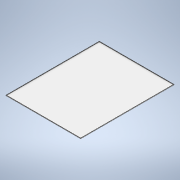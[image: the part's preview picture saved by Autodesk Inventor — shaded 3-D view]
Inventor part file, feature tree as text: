
AUTODESK INVENTOR PART (.ipt)
format: ipt  version: 2021 (Build 250183000, 183)  size: 107,520 bytes
history: native  units: mm
features: extrude x2, sketch x2
ambient origin geometry x8: Origin, YZ Plane, XZ Plane, XY Plane, X Axis, Y Axis, Z Axis, Center Point
bodies: Solid1 (feature_tree)
feature tree (4):
  extrude  "Extrusion1"  Depth=1600.0mm
  extrude  "Extrusion2"  Depth=5.0mm
  sketch  "Sketch1"  dims[d0=2000.0mm d1=1600.0mm]
  sketch  "Sketch2"  dims[d2=12.0mm d3=0.0mm d4=5.0mm d5=10.0mm d6=0.0mm]
